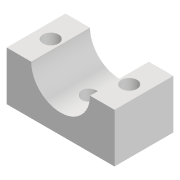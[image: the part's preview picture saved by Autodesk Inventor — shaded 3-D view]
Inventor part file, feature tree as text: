
AUTODESK INVENTOR PART (.ipt)
format: ipt  version: 2022 (Build 260153000, 153)  size: 119,296 bytes
history: native  units: mm
features: extrude x3, sketch x3
ambient origin geometry x8: Origin, YZ Plane, XZ Plane, XY Plane, X Axis, Y Axis, Z Axis, Center Point
bodies: Solid1 (feature_tree)
feature tree (6):
  extrude  "Extrusion1"  Depth=11.0mm
  extrude  "Extrusion2"  Depth=10.0mm
  extrude  "Extrusion3"  Depth=10.0mm TaperAngle=0.0deg
  sketch  "Sketch2"  dims[d0=12.0mm d1=11.0mm]
  sketch  "Sketch3"  dims[d2=11.0mm d3=10.0mm]
  sketch  "Sketch4"  dims[d4=3.0mm d5=12.0mm d6=0.0mm d7=3.2mm d8=3.0mm d9=6.0mm d10=3.2mm d11=3.0mm d12=6.0mm d13=10.0mm d14=0.0mm d15=3.1mm d16=6.0mm d17=10.0mm d18=0.0mm]
